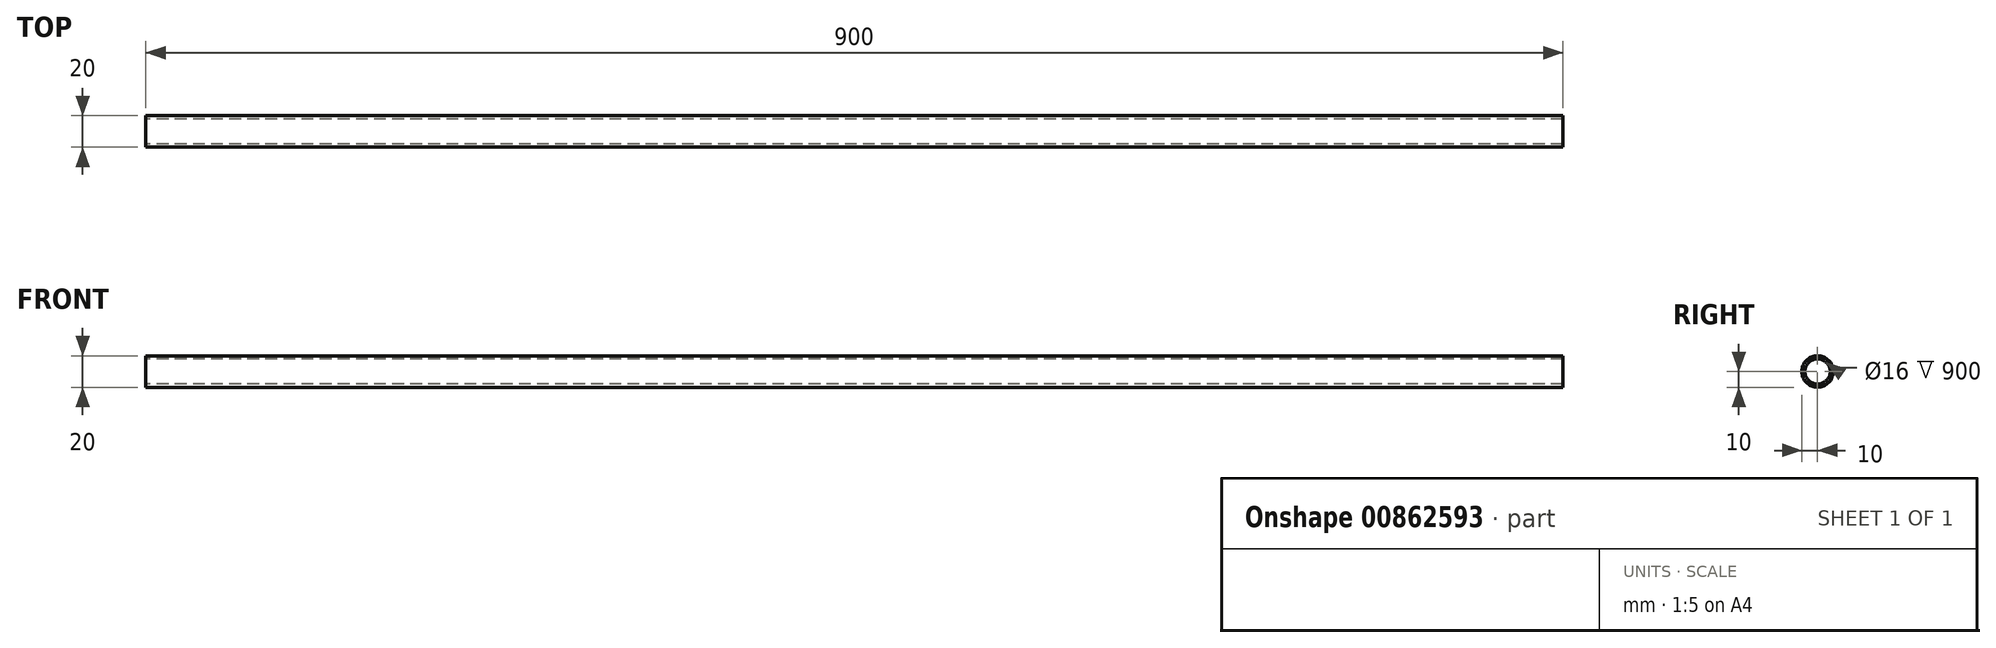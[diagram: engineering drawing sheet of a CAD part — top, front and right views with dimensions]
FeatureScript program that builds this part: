
annotation { "Feature Type Name" : "Feature", "Feature Type Description" : "" }
export const myFeature = defineFeature(function(context is Context, id is Id, definition is map)
    precondition{}
    {
        {
            var Q0;
            Q0=qCreatedBy(makeId("Front.planeOp"),FACE);
            var sketch = newSketch(context, id + "F0", { "sketchPlane" : qUnion([Q0])});
            skLineSegment(sketch, "E0", {"start": v(0, 0) * mm, "end": v(-900, 0) * mm});
            skSolve(sketch);
        }
        {
            var Q0;
            Q0=qCreatedBy(makeId("Right.planeOp"),FACE);
            var sketch = newSketch(context, id + "F1", { "sketchPlane" : qUnion([Q0])});
            skCircle(sketch, "E1", {"center": v(0, 0) * mm, "radius": 10 * mm});
            skCircle(sketch, "E2.0", {"center": v(0, 0) * mm, "radius": 8 * mm});
            skSolve(sketch);
        }
        {
            var Q0;
            Q0=makeQuery(id+"F1.imprint","IMPRINT",FACE,{"disambiguationData":[TD([[makeQuery(id+"F1.imprint","IMPRINT",EDGE,{"derivedFrom":sQuery(id+"F1.wireOp",EDGE,"E1")}),1.0]])]});
            var Q1;
            Q1=qSketchRegion(id+"F0",true);
            var Q2;
            Q2=sQuery(id+"F0.wireOp",EDGE,"E0");
            var Q3;
            Q3=sQuery(id+"F0.wireOp",EDGE,"p5A3UMdK-bUuJ-hKgG-gMdl-WLMVe5IsXQ4y");
            var Q4;
            Q4=sQuery(id+"F0.wireOp",EDGE,"jqzmJtes-IEFJ-0xae-phxS-a4aVOckqLKgL");
            sweep(context, id + "F2", {"profiles" : qUnion([Q0, Q1]), "path" : qUnion([Q2, Q3, Q4])});
        }
    });
